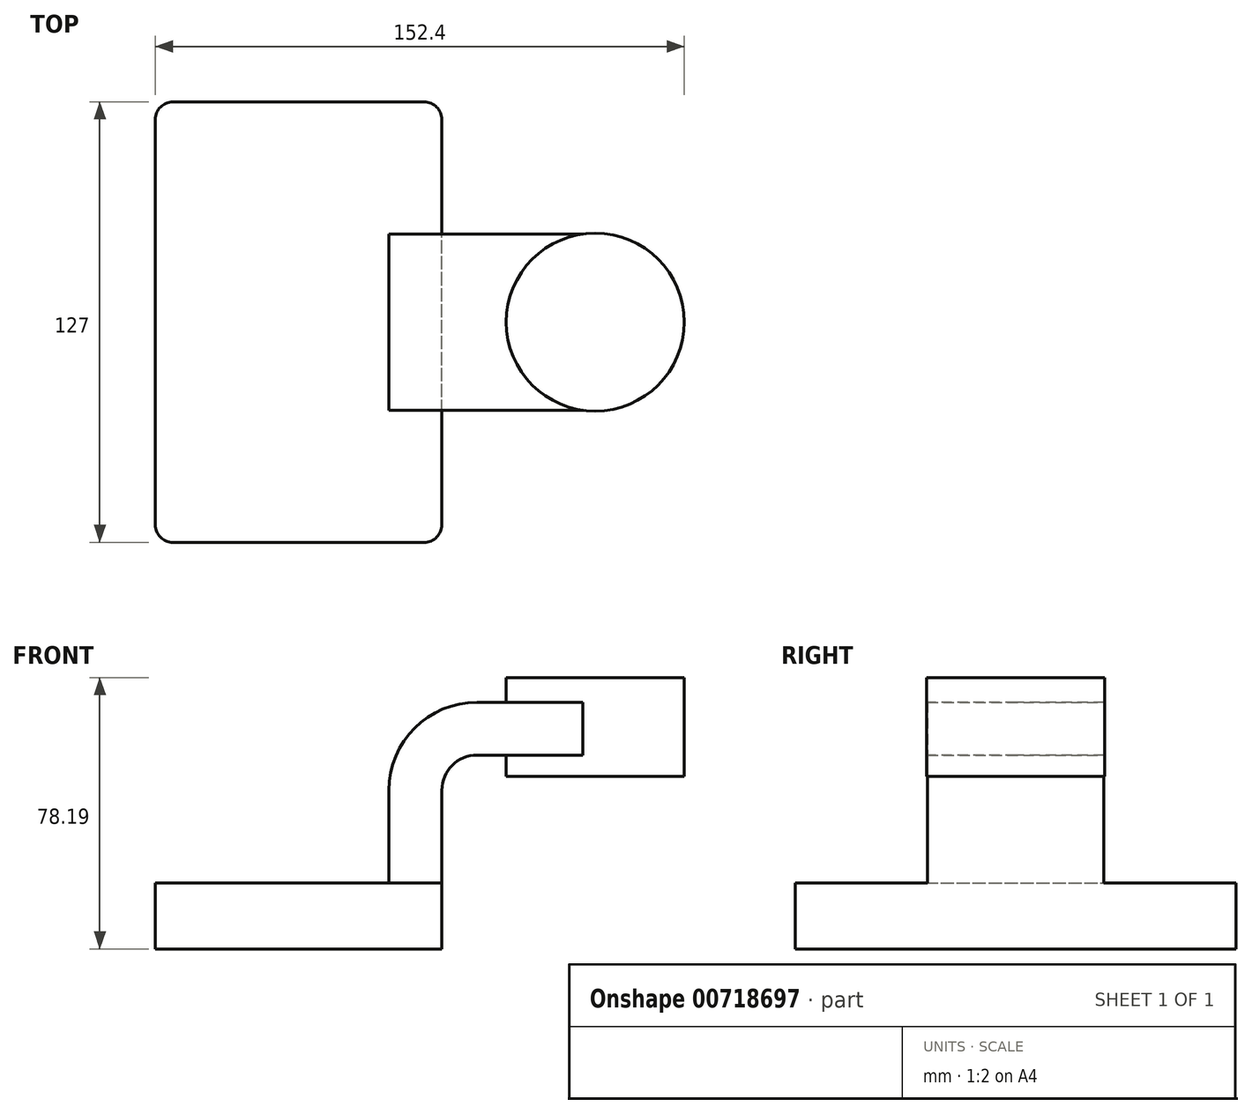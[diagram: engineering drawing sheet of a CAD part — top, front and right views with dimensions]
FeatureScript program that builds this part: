
annotation { "Feature Type Name" : "Feature", "Feature Type Description" : "" }
export const myFeature = defineFeature(function(context is Context, id is Id, definition is map)
    precondition{}
    {
        {
            var Q0;
            Q0=qCreatedBy(makeId("Front.planeOp"),FACE);
            var sketch = newSketch(context, id + "F0", { "sketchPlane" : qUnion([Q0])});
            skLineSegment(sketch, "E0.bottom", {"start": v(41.28, -9.52) * mm, "end": v(-41.28, -9.53) * mm});
            skLineSegment(sketch, "E0.top", {"start": v(41.28, 9.53) * mm, "end": v(-41.28, 9.53) * mm});
            skLineSegment(sketch, "E0.left", {"start": v(41.28, -9.52) * mm, "end": v(41.28, 9.53) * mm});
            skLineSegment(sketch, "E0.right", {"start": v(-41.28, -9.53) * mm, "end": v(-41.28, 9.53) * mm});
            skPoint(sketch, "E0.middle", {"position": v(0, 0) * mm});
            skLineSegment(sketch, "E1.bottom", {"start": v(111.12, 40.21) * mm, "end": v(60.32, 40.21) * mm});
            skLineSegment(sketch, "E1.top", {"start": v(111.12, 68.66) * mm, "end": v(60.32, 68.66) * mm});
            skLineSegment(sketch, "E1.left", {"start": v(111.12, 40.21) * mm, "end": v(111.12, 68.66) * mm});
            skLineSegment(sketch, "E1.right", {"start": v(60.32, 40.21) * mm, "end": v(60.32, 68.66) * mm});
            skPoint(sketch, "E1.middle", {"position": v(85.72, 54.44) * mm});
            skLineSegment(sketch, "E2", {"start": v(41.28, 9.53) * mm, "end": v(41.28, 36.2) * mm});
            skArc(sketch, "E3", {"start": v(41.27, 36.2) * mm, "mid": v(44.25, 43.38) * mm, "end": v(51.44, 46.36) * mm});
            skLineSegment(sketch, "E4", {"start": v(51.44, 46.36) * mm, "end": v(85.47, 46.36) * mm});
            skLineSegment(sketch, "E5.0", {"start": v(51.44, 61.6) * mm, "end": v(85.47, 61.6) * mm});
            skArc(sketch, "E5.1", {"start": v(26.04, 36.2) * mm, "mid": v(33.47, 54.16) * mm, "end": v(51.44, 61.6) * mm});
            skLineSegment(sketch, "E5.2", {"start": v(26.04, 9.53) * mm, "end": v(26.04, 36.2) * mm});
            skLineSegment(sketch, "E6", {"start": v(85.47, 46.36) * mm, "end": v(85.47, 68.66) * mm});
            skFitSpline(sketch, "E7", {"points": [v(-41.28, 9.53) * mm, v(51.44, 61.6) * mm], "startDerivative": vector(50.24, 104.92) * mm, "endDerivative": vector(147.44, -1.72) * mm});
            skLineSegment(sketch, "E8", {"start": v(85.47, 46.36) * mm, "end": v(85.47, 40.21) * mm});
            skPoint(sketch, "E8.endSnap0", {"position": v(85.72, 40.21) * mm});
            skSolve(sketch);
        }
        {
            var Q0;
            Q0=makeQuery(id+"F0.imprint","IMPRINT",FACE,{"disambiguationData":[TD([[makeQuery(id+"F0.imprint","IMPRINT",EDGE,{"derivedFrom":sQuery(id+"F0.wireOp",EDGE,"E0.bottom")}),-1.0]])]});
            extrude(context, id + "F1", {"entities" : qUnion([Q0]), "depth" : 127 * mm, "offsetDistance" : 25.4 * mm, "symmetric" : true});
        }
        {
            var Q0;
            {var subQ1=sQuery(id+"F0.wireOp",EDGE,"E2");Q0=makeQuery(id+"F0.imprint","IMPRINT",FACE,{"disambiguationData":[TD([[makeQuery(id+"F0.imprint","IMPRINT",EDGE,{"derivedFrom":subQ1}),1.0]])]});}
            var Q1;
            {var subQ0=sQuery(id+"F0.wireOp",EDGE,"E4");var subQ1=sQuery(id+"F0.wireOp",EDGE,"E1.right");var subQ2=makeQuery(id+"F0.imprint","INTERSECT",VERTEX,{"derivedFrom":[subQ1,subQ0]});Q1=makeQuery(id+"F0.imprint","IMPRINT",FACE,{"disambiguationData":[TD([[makeQuery(id+"F0.imprint","IMPRINT",EDGE,{"disambiguationData":[TD([[subQ2,-1.0]])],"derivedFrom":subQ1}),-1.0]])]});}
            extrude(context, id + "F2", {"entities" : qUnion([Q0, Q1]), "operationType" : NewBodyOperationType.ADD, "depth" : 50.8 * mm, "offsetDistance" : 25.4 * mm, "symmetric" : true});
        }
        {
            var Q0;
            Q0=makeQuery(id+"F0.imprint","IMPRINT",FACE,{"disambiguationData":[TD([[makeQuery(id+"F0.imprint","IMPRINT",EDGE,{"derivedFrom":sQuery(id+"F0.wireOp",EDGE,"E5.1")}),1.0]])]});
            extrude(context, id + "F3", {"entities" : qUnion([Q0]), "operationType" : NewBodyOperationType.ADD, "depth" : 15.24 * mm, "offsetDistance" : 25.4 * mm, "symmetric" : true});
        }
        {
            var Q0;
            {var subQ3=sQuery(id+"F0.wireOp",EDGE,"E1.left");Q0=makeQuery(id+"F0.imprint","IMPRINT",FACE,{"disambiguationData":[TD([[makeQuery(id+"F0.imprint","IMPRINT",EDGE,{"derivedFrom":subQ3}),1.0]])]});}
            var Q1;
            Q1=sQuery(id+"F0.wireOp",EDGE,"E6");
            revolve(context, id + "F4", {"operationType" : NewBodyOperationType.ADD, "surfaceOperationType" : NewSurfaceOperationType.NEW, "entities" : qUnion([Q0]), "axis" : qUnion([Q1]), "revolveType" : RevolveType.FULL});
        }
        {
            var Q0;
            Q0=makeQuery(id+"F1.opExtrude","CAP_EDGE",EDGE,{"disambiguationData":[OSD([sQuery(id+"F0.wireOp",EDGE,"E0.left")])],"isStart":false});
            fillet(context, id + "F5", {"entities" : qUnion([Q0]), "radius" : 5.08 * mm, "tangentPropagation" : true, "allowEdgeOverflow" : false});
        }
        {
            var Q0;
            Q0=makeQuery(id+"F1.opExtrude","CAP_EDGE",EDGE,{"disambiguationData":[OSD([sQuery(id+"F0.wireOp",EDGE,"E0.right")])],"isStart":false});
            fillet(context, id + "F6", {"entities" : qUnion([Q0]), "radius" : 5.08 * mm, "tangentPropagation" : true, "allowEdgeOverflow" : false});
        }
        {
            var Q0;
            Q0=makeQuery(id+"F1.opExtrude","CAP_EDGE",EDGE,{"disambiguationData":[OSD([sQuery(id+"F0.wireOp",EDGE,"E0.left")])],"isStart":true});
            fillet(context, id + "F7", {"entities" : qUnion([Q0]), "radius" : 5.08 * mm, "tangentPropagation" : true, "allowEdgeOverflow" : false});
        }
        {
            var Q0;
            Q0=makeQuery(id+"F1.opExtrude","CAP_EDGE",EDGE,{"disambiguationData":[OSD([sQuery(id+"F0.wireOp",EDGE,"E0.right")])],"isStart":true});
            fillet(context, id + "F8", {"entities" : qUnion([Q0]), "radius" : 5.08 * mm, "tangentPropagation" : true, "allowEdgeOverflow" : false});
        }
    });
